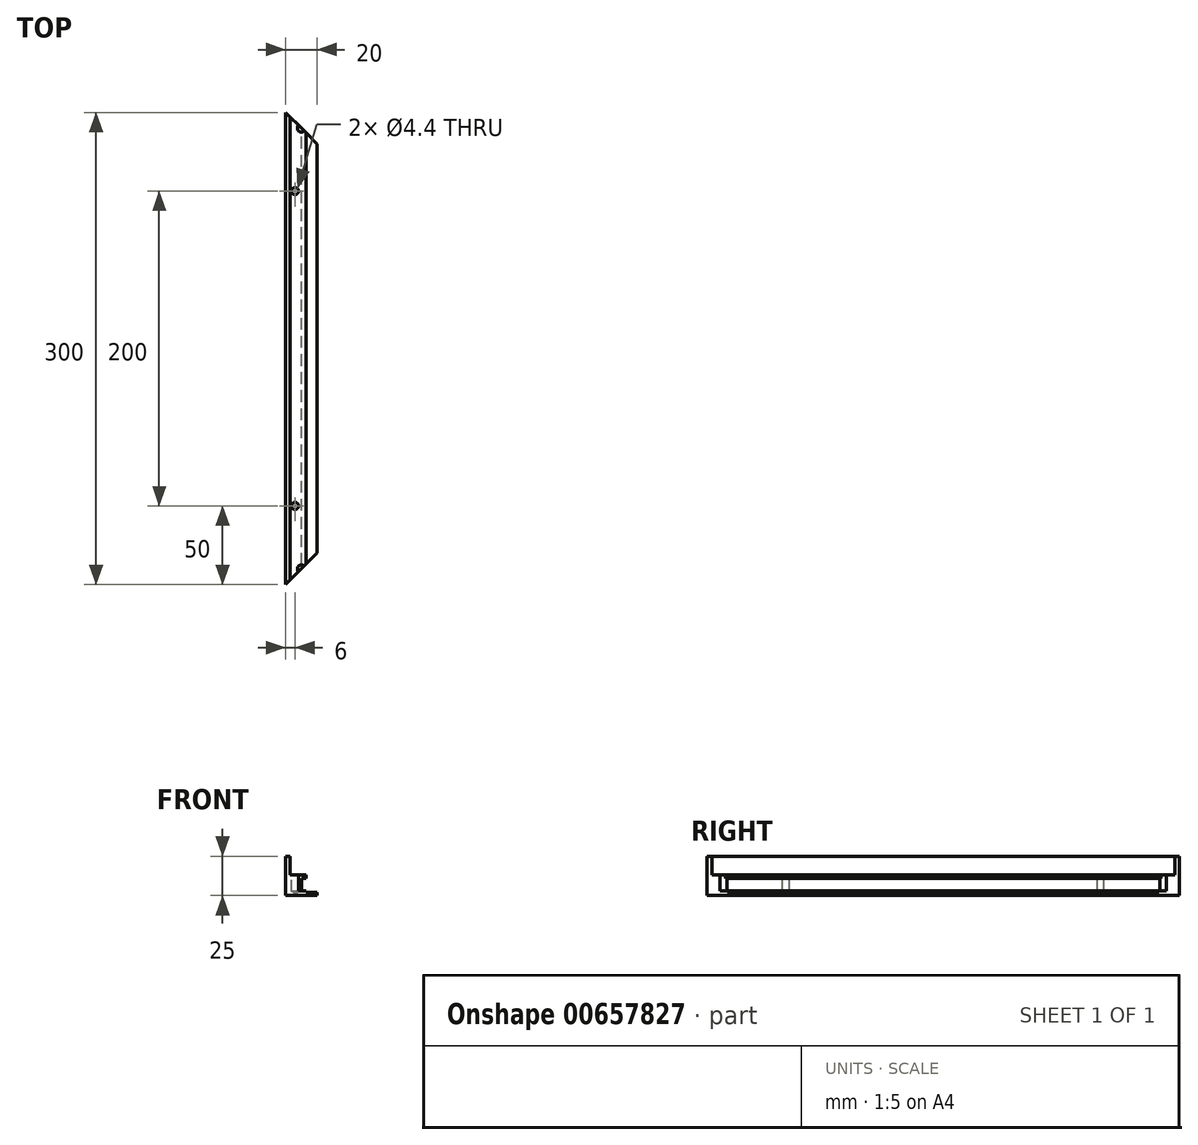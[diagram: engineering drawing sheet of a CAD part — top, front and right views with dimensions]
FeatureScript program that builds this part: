
annotation { "Feature Type Name" : "Feature", "Feature Type Description" : "" }
export const myFeature = defineFeature(function(context is Context, id is Id, definition is map)
    precondition{}
    {
        {
            var Q0;
            Q0=qCreatedBy(makeId("Front.planeOp"),FACE);
            var sketch = newSketch(context, id + "F0", { "sketchPlane" : qUnion([Q0])});
            skLineSegment(sketch, "E0.bottom", {"start": v(0, 0) * mm, "end": v(-10, 0) * mm});
            skLineSegment(sketch, "E0.top", {"start": v(0, -10) * mm, "end": v(-10, -10) * mm});
            skLineSegment(sketch, "E0.left", {"start": v(0, 0) * mm, "end": v(0, -10) * mm});
            skLineSegment(sketch, "E0.right", {"start": v(-10, 0) * mm, "end": v(-10, -10) * mm});
            skLineSegment(sketch, "E1.bottom", {"start": v(0, -10) * mm, "end": v(3, -10) * mm});
            skLineSegment(sketch, "E1.top", {"start": v(0, -8) * mm, "end": v(3, -8) * mm});
            skLineSegment(sketch, "E1.left", {"start": v(0, -10) * mm, "end": v(0, -8) * mm});
            skLineSegment(sketch, "E1.right", {"start": v(3, -10) * mm, "end": v(3, -8) * mm});
            skLineSegment(sketch, "E2.bottom", {"start": v(3, -10) * mm, "end": v(10, -10) * mm});
            skLineSegment(sketch, "E2.top", {"start": v(3, -9) * mm, "end": v(10, -9) * mm});
            skLineSegment(sketch, "E2.left", {"start": v(3, -10) * mm, "end": v(3, -9) * mm});
            skLineSegment(sketch, "E2.right", {"start": v(10, -10) * mm, "end": v(10, -9) * mm});
            skLineSegment(sketch, "E3.bottom", {"start": v(-10, 0) * mm, "end": v(3, 0) * mm});
            skLineSegment(sketch, "E3.top", {"start": v(-10, 2) * mm, "end": v(3, 2) * mm});
            skLineSegment(sketch, "E3.left", {"start": v(-10, 0) * mm, "end": v(-10, 2) * mm});
            skLineSegment(sketch, "E3.right", {"start": v(3, 0) * mm, "end": v(3, 2) * mm});
            skLineSegment(sketch, "E4.bottom", {"start": v(-10, 2) * mm, "end": v(-7, 2) * mm});
            skLineSegment(sketch, "E4.top", {"start": v(-10, 14) * mm, "end": v(-7, 14) * mm});
            skLineSegment(sketch, "E4.left", {"start": v(-10, 2) * mm, "end": v(-10, 14) * mm});
            skLineSegment(sketch, "E4.right", {"start": v(-7, 2) * mm, "end": v(-7, 14) * mm});
            skLineSegment(sketch, "E5.bottom", {"start": v(-10, -10) * mm, "end": v(10, -10) * mm});
            skLineSegment(sketch, "E5.top", {"start": v(-10, -11) * mm, "end": v(10, -11) * mm});
            skLineSegment(sketch, "E5.left", {"start": v(-10, -10) * mm, "end": v(-10, -11) * mm});
            skLineSegment(sketch, "E5.right", {"start": v(10, -10) * mm, "end": v(10, -11) * mm});
            skSolve(sketch);
        }
        {
            var Q0;
            Q0=makeQuery(id+"F0.imprint","IMPRINT",FACE,{"disambiguationData":[TD([[makeQuery(id+"F0.imprint","IMPRINT",EDGE,{"derivedFrom":sQuery(id+"F0.wireOp",EDGE,"E4.top")}),-1.0]])]});
            var Q1;
            Q1=makeQuery(id+"F0.imprint","IMPRINT",FACE,{"disambiguationData":[TD([[makeQuery(id+"F0.imprint","IMPRINT",EDGE,{"derivedFrom":sQuery(id+"F0.wireOp",EDGE,"E0.bottom")}),-1.0]])]});
            var Q2;
            {var subQ3=sQuery(id+"F0.wireOp",EDGE,"E0.bottom");Q2=makeQuery(id+"F0.imprint","IMPRINT",FACE,{"disambiguationData":[TD([[makeQuery(id+"F0.imprint","IMPRINT",EDGE,{"derivedFrom":subQ3}),1.0]])]});}
            var Q3;
            Q3=makeQuery(id+"F0.imprint","IMPRINT",FACE,{"disambiguationData":[TD([[makeQuery(id+"F0.imprint","IMPRINT",EDGE,{"derivedFrom":sQuery(id+"F0.wireOp",EDGE,"E0.top")}),1.0]])]});
            var Q4;
            {var subQ0=sQuery(id+"F0.wireOp",EDGE,"E2.bottom");Q4=makeQuery(id+"F0.imprint","IMPRINT",FACE,{"disambiguationData":[TD([[makeQuery(id+"F0.imprint","IMPRINT",EDGE,{"derivedFrom":subQ0}),1.0]])]});}
            var Q5;
            {var subQ1=sQuery(id+"F0.wireOp",EDGE,"E1.bottom");Q5=makeQuery(id+"F0.imprint","IMPRINT",FACE,{"disambiguationData":[TD([[makeQuery(id+"F0.imprint","IMPRINT",EDGE,{"derivedFrom":subQ1}),1.0]])]});}
            extrude(context, id + "F1", {"entities" : qUnion([Q0, Q1, Q2, Q3, Q4, Q5]), "depth" : 150 * mm, "offsetDistance" : 25 * mm});
        }
        {
            var Q0;
            Q0=makeQuery(id+"F1.opExtrude","SWEPT_FACE",FACE,{"disambiguationData":[OSD([sQuery(id+"F0.wireOp",EDGE,"E3.top")])]});
            var sketch = newSketch(context, id + "F2", { "sketchPlane" : qUnion([Q0])});
            skLineSegment(sketch, "E6", {"start": v(-2, -150) * mm, "end": v(-2, -100) * mm});
            skLineSegment(sketch, "E7", {"start": v(-2, -100) * mm, "end": v(-4, -100) * mm});
            skCircle(sketch, "E8", {"center": v(-4, -100) * mm, "radius": 2 * mm});
            skSolve(sketch);
        }
        {
            var Q0;
            Q0=sQuery(id+"F2.wireOp",VERTEX,"E8.center");
            var Q1;
            Q1=makeQuery(id+"F1.opExtrude","SWEPT_BODY",BODY,{"disambiguationData":[OSD([sQuery(id+"F0.wireOp",EDGE,"E0.left"),sQuery(id+"F0.wireOp",EDGE,"E0.right"),sQuery(id+"F0.wireOp",EDGE,"E1.top"),sQuery(id+"F0.wireOp",EDGE,"E1.right"),sQuery(id+"F0.wireOp",EDGE,"E2.top"),sQuery(id+"F0.wireOp",EDGE,"E2.right"),sQuery(id+"F0.wireOp",EDGE,"E3.bottom"),sQuery(id+"F0.wireOp",EDGE,"E3.top"),sQuery(id+"F0.wireOp",EDGE,"E3.left"),sQuery(id+"F0.wireOp",EDGE,"E3.right"),sQuery(id+"F0.wireOp",EDGE,"E4.top"),sQuery(id+"F0.wireOp",EDGE,"E4.left"),sQuery(id+"F0.wireOp",EDGE,"E4.right"),sQuery(id+"F0.wireOp",EDGE,"E5.top"),sQuery(id+"F0.wireOp",EDGE,"E5.left"),sQuery(id+"F0.wireOp",EDGE,"E5.right")])]});
            hole(context, id + "F3", {"style" : HoleStyle.SIMPLE, "endStyle" : HoleEndStyle.BLIND, "standardTappedOrClearance" : lookupTablePath({ "standard" : "ISO", "fit" : "Normal", "size" : "M4", "type" : "Clearance" }), "standardBlindInLast" : lookupTablePath({ "fit" : "Standard", "standard" : "ISO", "size" : "M4", "type" : "Clearance" }), "holeDiameter" : 4.4 * mm, "majorDiameter" : 5 * mm, "holeDepth" : 10.4 * mm, "isTappedThrough" : true, "tappedDepth" : 8 * mm, "tapClearance" : 3, "locations" : qUnion([Q0]), "scope" : qUnion([Q1])});
        }
        {
            var Q0;
            Q0=makeQuery(id+"F1.opExtrude","CAP_EDGE",EDGE,{"disambiguationData":[OSD([sQuery(id+"F0.wireOp",EDGE,"E2.right"),sQuery(id+"F0.wireOp",EDGE,"E5.right")])],"isStart":false});
            chamfer(context, id + "F4", {"entities" : qUnion([Q0]), "width" : 20 * mm, "tangentPropagation" : true});
        }
        {
            var Q0;
            Q0=makeQuery(id+"F1.opExtrude","SWEPT_FACE",FACE,{"disambiguationData":[OSD([sQuery(id+"F0.wireOp",EDGE,"E3.bottom")])]});
            var sketch = newSketch(context, id + "F5", { "sketchPlane" : qUnion([Q0])});
            skCircle(sketch, "E9", {"center": v(0, 140) * mm, "radius": 2.5 * mm});
            skSolve(sketch);
        }
        {
            var Q0;
            {var subQ0=sQuery(id+"F5.wireOp",EDGE,"E9");var subQ1=sQuery(id+"F0.wireOp",EDGE,"E3.bottom");var subQ2=makeQuery(id+"F1.opExtrude","SWEPT_EDGE",EDGE,{"disambiguationData":[OSD([sQuery(id+"F0.wireOp",EDGE,"E0.bottom"),sQuery(id+"F0.wireOp",EDGE,"E0.left"),subQ1])]});var subQ3=makeQuery(id+"F5.imprint","INTERSECT",VERTEX,{"derivedFrom":[subQ2,subQ0]});Q0=makeQuery(id+"F5.imprint","IMPRINT",FACE,{"disambiguationData":[TD([[makeQuery(id+"F5.imprint","IMPRINT",EDGE,{"disambiguationData":[TD([[subQ3,1.0]])],"derivedFrom":subQ0}),1.0]])]});}
            var Q1;
            {var subQ0=sQuery(id+"F5.wireOp",EDGE,"E9");var subQ1=sQuery(id+"F0.wireOp",EDGE,"E3.bottom");var subQ2=makeQuery(id+"F1.opExtrude","SWEPT_EDGE",EDGE,{"disambiguationData":[OSD([sQuery(id+"F0.wireOp",EDGE,"E0.bottom"),sQuery(id+"F0.wireOp",EDGE,"E0.left"),subQ1])]});var subQ3=makeQuery(id+"F5.imprint","INTERSECT",VERTEX,{"derivedFrom":[subQ2,subQ0]});Q1=makeQuery(id+"F5.imprint","IMPRINT",FACE,{"disambiguationData":[TD([[makeQuery(id+"F5.imprint","IMPRINT",EDGE,{"disambiguationData":[TD([[subQ3,-1.0]])],"derivedFrom":subQ0}),1.0]])]});}
            var Q2;
            Q2=sQuery(id+"F5.wireOp",EDGE,"E9");
            extrude(context, id + "F6", {"entities" : qUnion([Q0, Q1]), "operationType" : NewBodyOperationType.REMOVE, "surfaceEntities" : qUnion([Q2]), "endBound" : BoundingType.SYMMETRIC, "oppositeDirection" : true, "depth" : 16 * mm, "offsetDistance" : 25 * mm});
        }
        {
            var Q0;
            Q0=makeQuery(id+"F1.opExtrude","SWEPT_BODY",BODY,{"disambiguationData":[OSD([sQuery(id+"F0.wireOp",EDGE,"E0.left"),sQuery(id+"F0.wireOp",EDGE,"E0.right"),sQuery(id+"F0.wireOp",EDGE,"E1.top"),sQuery(id+"F0.wireOp",EDGE,"E1.right"),sQuery(id+"F0.wireOp",EDGE,"E2.top"),sQuery(id+"F0.wireOp",EDGE,"E2.right"),sQuery(id+"F0.wireOp",EDGE,"E3.bottom"),sQuery(id+"F0.wireOp",EDGE,"E3.top"),sQuery(id+"F0.wireOp",EDGE,"E3.left"),sQuery(id+"F0.wireOp",EDGE,"E3.right"),sQuery(id+"F0.wireOp",EDGE,"E4.top"),sQuery(id+"F0.wireOp",EDGE,"E4.left"),sQuery(id+"F0.wireOp",EDGE,"E4.right"),sQuery(id+"F0.wireOp",EDGE,"E5.top"),sQuery(id+"F0.wireOp",EDGE,"E5.left"),sQuery(id+"F0.wireOp",EDGE,"E5.right")])]});
            var Q1;
            Q1=makeQuery(id+"F1.opExtrude","CAP_FACE",FACE,{"disambiguationData":[OSD([sQuery(id+"F0.wireOp",EDGE,"E0.left"),sQuery(id+"F0.wireOp",EDGE,"E0.right"),sQuery(id+"F0.wireOp",EDGE,"E1.top"),sQuery(id+"F0.wireOp",EDGE,"E1.right"),sQuery(id+"F0.wireOp",EDGE,"E2.top"),sQuery(id+"F0.wireOp",EDGE,"E2.right"),sQuery(id+"F0.wireOp",EDGE,"E3.bottom"),sQuery(id+"F0.wireOp",EDGE,"E3.top"),sQuery(id+"F0.wireOp",EDGE,"E3.left"),sQuery(id+"F0.wireOp",EDGE,"E3.right"),sQuery(id+"F0.wireOp",EDGE,"E4.top"),sQuery(id+"F0.wireOp",EDGE,"E4.left"),sQuery(id+"F0.wireOp",EDGE,"E4.right"),sQuery(id+"F0.wireOp",EDGE,"E5.top"),sQuery(id+"F0.wireOp",EDGE,"E5.left"),sQuery(id+"F0.wireOp",EDGE,"E5.right")])],"isStart":true});
            mirror(context, id + "F7", {"operationType" : NewBodyOperationType.ADD, "entities" : qUnion([Q0]), "mirrorPlane" : qUnion([Q1])});
        }
    });
